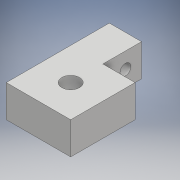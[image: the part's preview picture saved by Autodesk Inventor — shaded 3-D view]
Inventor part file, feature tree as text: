
AUTODESK INVENTOR PART (.ipt)
format: ipt  version: 2017 (Build 210142000, 142)  size: 221,184 bytes
history: native  units: mm
features: extrude x2, sketch x2
ambient origin geometry x8: Origin, YZ Plane, XZ Plane, XY Plane, X Axis, Y Axis, Z Axis, Center Point
bodies: Body1 (feature_tree)
feature tree (4):
  extrude  "押し出し4"  Depth=20.0mm
  extrude  "押し出し5"  Depth=32.0mm
  sketch  "スケッチ4"
  sketch  "スケッチ5"
